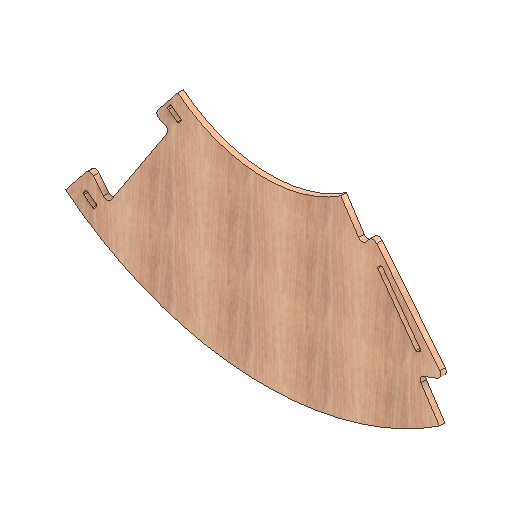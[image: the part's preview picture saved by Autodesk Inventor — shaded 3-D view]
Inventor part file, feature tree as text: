
AUTODESK INVENTOR PART (.ipt)
format: ipt  version: 2021 (Build 250183000, 183)  size: 278,016 bytes
history: native  units: mm
features: other x2, extrude x2, hole x1
ambient origin geometry x8: Origin, YZ Plane, XZ Plane, XY Plane, X Axis, Y Axis, Z Axis, Center Point
bodies: Solid1 (feature_tree)
feature tree (5):
  other  "CONTOURS"
  hole  "HOLES"  [1 undecoded]
  other  "LETTERS"
  extrude  "Extrusion1"  Depth=18.0mm TaperAngle=0.0deg
  extrude  "Extrusion2"  [1 undecoded]
note: 2 required parameter values undecoded (feature->parameter linkage not recoverable at this tier; creation-order binding heuristic only, values carry confidence <= 0.55)
